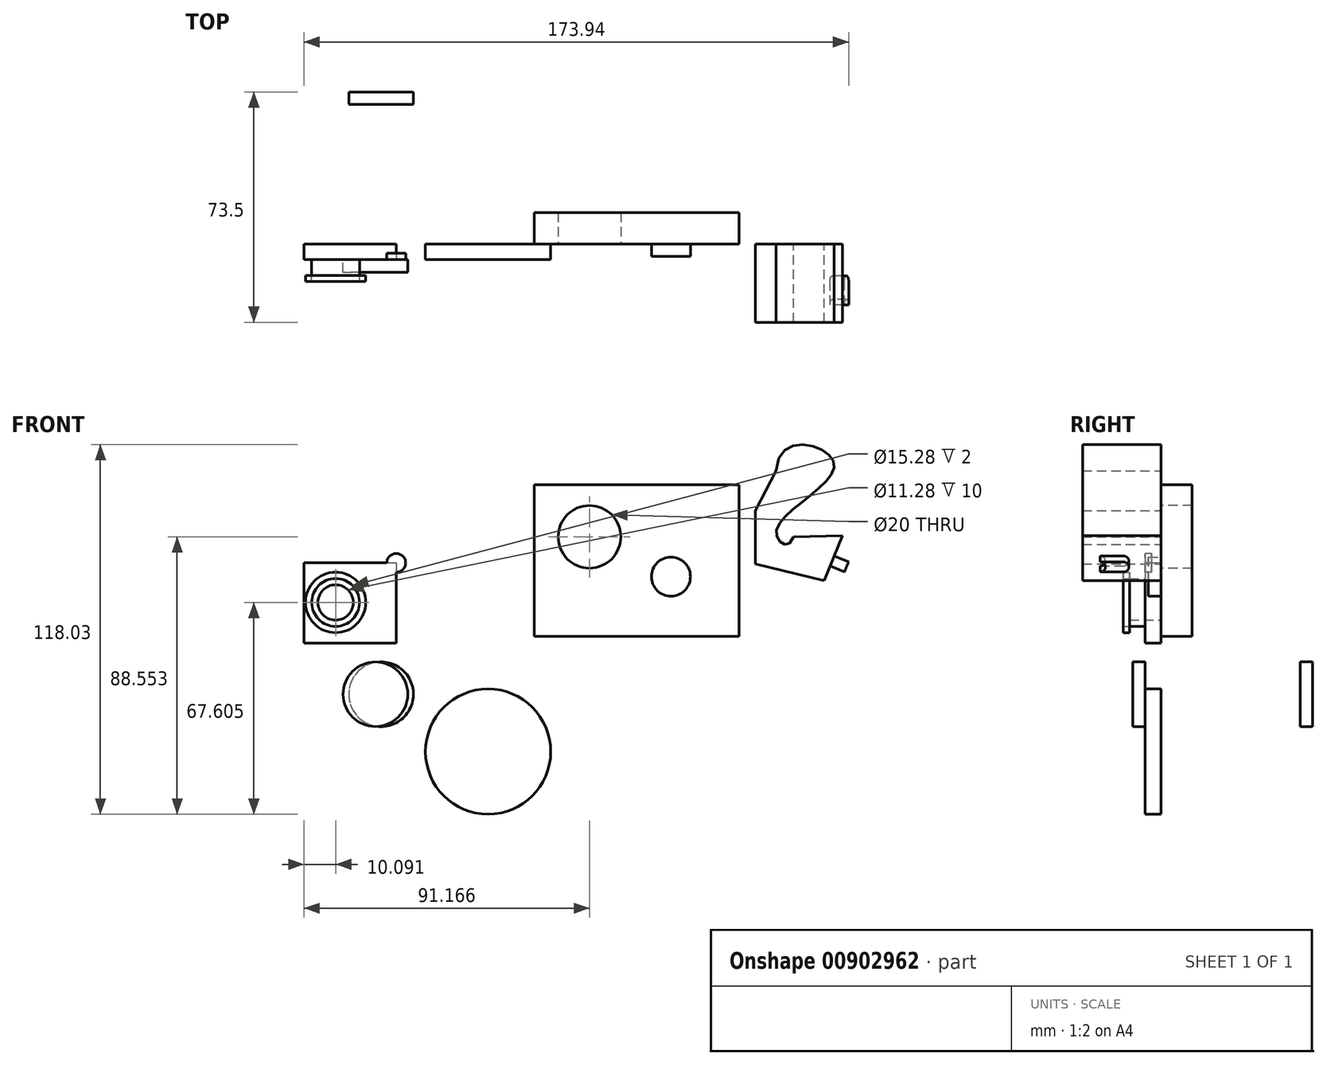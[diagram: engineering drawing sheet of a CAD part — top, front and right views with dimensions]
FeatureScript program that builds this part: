
annotation { "Feature Type Name" : "Feature", "Feature Type Description" : "" }
export const myFeature = defineFeature(function(context is Context, id is Id, definition is map)
    precondition{}
    {
        {
            var Q0;
            Q0=qCreatedBy(makeId("Front.planeOp"),FACE);
            var sketch = newSketch(context, id + "F0", { "sketchPlane" : qUnion([Q0])});
            skLineSegment(sketch, "E0.bottom", {"start": v(-53.56, 35.43) * mm, "end": v(11.78, 35.43) * mm});
            skLineSegment(sketch, "E0.top", {"start": v(-53.56, -12.9) * mm, "end": v(11.78, -12.9) * mm});
            skLineSegment(sketch, "E0.left", {"start": v(-53.56, 35.43) * mm, "end": v(-53.56, -12.9) * mm});
            skLineSegment(sketch, "E0.right", {"start": v(11.78, 35.43) * mm, "end": v(11.78, -12.9) * mm});
            skCircle(sketch, "E1", {"center": v(-35.94, 18.84) * mm, "radius": 10 * mm});
            skSolve(sketch);
        }
        {
            var Q0;
            Q0=makeQuery(id+"F0.imprint","IMPRINT",FACE,{"disambiguationData":[TD([[makeQuery(id+"F0.imprint","IMPRINT",EDGE,{"derivedFrom":sQuery(id+"F0.wireOp",EDGE,"E0.bottom")}),-1.0]])]});
            extrude(context, id + "F1", {"entities" : qUnion([Q0]), "depth" : -10 * mm, "offsetDistance" : 25 * mm});
        }
        {
            var Q0;
            Q0=qCreatedBy(makeId("Front.planeOp"),FACE);
            var sketch = newSketch(context, id + "F2", { "sketchPlane" : qUnion([Q0])});
            skCircle(sketch, "E2", {"center": v(-9.93, 6.14) * mm, "radius": 6.23 * mm});
            skSolve(sketch);
        }
        {
            var Q0;
            Q0=makeQuery(id+"F2.imprint","IMPRINT",FACE,{"disambiguationData":[TD([[makeQuery(id+"F2.imprint","IMPRINT",EDGE,{"derivedFrom":sQuery(id+"F2.wireOp",EDGE,"E2")}),1.0]])]});
            extrude(context, id + "F3", {"entities" : qUnion([Q0]), "operationType" : NewBodyOperationType.ADD, "depth" : 4 * mm, "offsetDistance" : 25 * mm});
        }
        {
            var Q0;
            Q0=qCreatedBy(makeId("Front.planeOp"),FACE);
            var sketch = newSketch(context, id + "F4", { "sketchPlane" : qUnion([Q0])});
            skFitSpline(sketch, "E3", {"points": [v(29.19, 18.84) * mm, v(23.66, 20.07) * mm, v(42.09, 42.6) * mm, v(23.66, 39.94) * mm], "startDerivative": vector(-20.54, -69.85) * mm, "endDerivative": vector(-5.4, -109.98) * mm});
            skLineSegment(sketch, "E4", {"start": v(23.66, 39.94) * mm, "end": v(17.05, 27.24) * mm});
            skLineSegment(sketch, "E5", {"start": v(17.05, 27.24) * mm, "end": v(17.05, 10.24) * mm});
            skLineSegment(sketch, "E6", {"start": v(17.05, 10.24) * mm, "end": v(38.96, 4.92) * mm});
            skLineSegment(sketch, "E7", {"start": v(38.96, 4.92) * mm, "end": v(44.9, 19.25) * mm});
            skLineSegment(sketch, "E8", {"start": v(44.9, 19.25) * mm, "end": v(29.19, 18.84) * mm});
            skSolve(sketch);
        }
        {
            var Q0;
            Q0=qCreatedBy(makeId("Front.planeOp"),FACE);
            var sketch = newSketch(context, id + "F5", { "sketchPlane" : qUnion([Q0])});
            skCircle(sketch, "E9", {"center": v(-68.32, -49.71) * mm, "radius": 20 * mm});
            skArc(sketch, "E10", {"start": v(38.29, -46.18) * mm, "mid": v(45.77, -34.95) * mm, "end": v(32.35, -33.48) * mm});
            skLineSegment(sketch, "E11", {"start": v(44.52, -43.53) * mm, "end": v(48.52, -43.53) * mm});
            skLineSegment(sketch, "E12", {"start": v(44.52, -43.53) * mm, "end": v(48.52, -40.53) * mm});
            skLineSegment(sketch, "E13", {"start": v(48.52, -40.53) * mm, "end": v(48.52, -43.53) * mm});
            skSolve(sketch);
        }
        {
            var Q0;
            Q0=makeQuery(id+"F4.imprint","IMPRINT",FACE,{"disambiguationData":[TD([[makeQuery(id+"F4.imprint","IMPRINT",EDGE,{"derivedFrom":sQuery(id+"F4.wireOp",EDGE,"E3")}),1.0]])]});
            extrude(context, id + "F6", {"entities" : qUnion([Q0]), "depth" : 5 * mm, "offsetDistance" : 25 * mm});
        }
        {
            var Q0;
            Q0=makeQuery(id+"F4.imprint","IMPRINT",FACE,{"disambiguationData":[TD([[makeQuery(id+"F4.imprint","IMPRINT",EDGE,{"derivedFrom":sQuery(id+"F4.wireOp",EDGE,"E3")}),1.0]])]});
            extrude(context, id + "F7", {"entities" : qUnion([Q0]), "operationType" : NewBodyOperationType.ADD, "depth" : 25 * mm, "offsetDistance" : 25 * mm});
        }
        {
            var Q0;
            {var subQ0=sQuery(id+"F4.wireOp",EDGE,"E7");Q0=makeQuery(id+"F7.boolean.opBoolean","MERGE",FACE,{"derivedFrom":[makeQuery(id+"F6.opExtrude","SWEPT_FACE",FACE,{"disambiguationData":[OSD([subQ0])]}),makeQuery(id+"F7.opExtrude","SWEPT_FACE",FACE,{"disambiguationData":[OSD([subQ0])]})]});}
            var sketch = newSketch(context, id + "F8", { "sketchPlane" : qUnion([Q0])});
            skLineSegment(sketch, "E14.bottom", {"start": v(-19.43, 27.93) * mm, "end": v(-11.94, 27.93) * mm});
            skLineSegment(sketch, "E14.top", {"start": v(-19.43, 24.45) * mm, "end": v(-11.94, 24.45) * mm});
            skLineSegment(sketch, "E14.right", {"start": v(-11.94, 27.93) * mm, "end": v(-11.94, 24.45) * mm});
            skArc(sketch, "E15", {"start": v(-11.94, 24.45) * mm, "mid": v(-10.2, 26.19) * mm, "end": v(-11.94, 27.93) * mm});
            skArc(sketch, "E16", {"start": v(-19.43, 24.45) * mm, "mid": v(-17.69, 26.19) * mm, "end": v(-19.43, 27.93) * mm});
            skSolve(sketch);
        }
        {
            var Q0;
            Q0=makeQuery(id+"F8.imprint","IMPRINT",FACE,{"disambiguationData":[TD([[makeQuery(id+"F8.imprint","IMPRINT",EDGE,{"derivedFrom":sQuery(id+"F8.wireOp",EDGE,"E14.right")}),1.0]])]});
            var Q1;
            Q1=makeQuery(id+"F8.imprint","IMPRINT",FACE,{"disambiguationData":[TD([[makeQuery(id+"F8.imprint","IMPRINT",EDGE,{"derivedFrom":sQuery(id+"F8.wireOp",EDGE,"E14.bottom")}),-1.0]])]});
            extrude(context, id + "F9", {"entities" : qUnion([Q0, Q1]), "operationType" : NewBodyOperationType.ADD, "depth" : 5 * mm, "offsetDistance" : 25 * mm});
        }
        {
            var Q0;
            Q0=qCreatedBy(makeId("Front.planeOp"),FACE);
            var sketch = newSketch(context, id + "F10", { "sketchPlane" : qUnion([Q0])});
            skLineSegment(sketch, "E17", {"start": v(-73.05, 50.1) * mm, "end": v(-17.22, 50.1) * mm});
            skPoint(sketch, "E18", {"position": v(-45.13, 50.1) * mm});
            skLineSegment(sketch, "E19", {"start": v(-17.22, 50.1) * mm, "end": v(-13.4, 59.93) * mm});
            skLineSegment(sketch, "E20.bottom", {"start": v(-73.05, 50.1) * mm, "end": v(-89.06, 50.1) * mm});
            skLineSegment(sketch, "E20.top", {"start": v(-73.05, 36.47) * mm, "end": v(-89.06, 36.47) * mm});
            skLineSegment(sketch, "E20.left", {"start": v(-73.05, 50.1) * mm, "end": v(-73.05, 36.47) * mm});
            skLineSegment(sketch, "E20.right", {"start": v(-89.06, 50.1) * mm, "end": v(-89.06, 36.47) * mm});
            skPoint(sketch, "E21", {"position": v(-81.05, 50.1) * mm});
            skPoint(sketch, "E22", {"position": v(-73.05, 43.29) * mm});
            skLineSegment(sketch, "E23", {"start": v(-89.06, 43.29) * mm, "end": v(-81.05, 36.47) * mm});
            skLineSegment(sketch, "E24", {"start": v(-81.05, 36.47) * mm, "end": v(-93.82, 21.48) * mm});
            skLineSegment(sketch, "E25", {"start": v(-89.06, 43.29) * mm, "end": v(-101.83, 28.3) * mm});
            skLineSegment(sketch, "E26", {"start": v(-93.82, 21.48) * mm, "end": v(-101.83, 28.3) * mm});
            skPoint(sketch, "E27", {"position": v(-101.83, 28.3) * mm});
            skLineSegment(sketch, "E28.bottom", {"start": v(-127.11, 10.53) * mm, "end": v(-97.65, 10.53) * mm});
            skLineSegment(sketch, "E28.top", {"start": v(-127.11, -15.1) * mm, "end": v(-97.65, -15.1) * mm});
            skLineSegment(sketch, "E28.left", {"start": v(-127.11, 10.53) * mm, "end": v(-127.11, -15.1) * mm});
            skLineSegment(sketch, "E28.right", {"start": v(-97.65, 10.53) * mm, "end": v(-97.65, -15.1) * mm});
            skCircle(sketch, "E29", {"center": v(-117.02, -2.1) * mm, "radius": 5.64 * mm});
            skSolve(sketch);
        }
        {
            var Q0;
            Q0=makeQuery(id+"F10.imprint","IMPRINT",FACE,{"disambiguationData":[TD([[makeQuery(id+"F10.imprint","IMPRINT",EDGE,{"derivedFrom":sQuery(id+"F10.wireOp",EDGE,"E28.bottom")}),-1.0]])]});
            extrude(context, id + "F11", {"entities" : qUnion([Q0]), "depth" : 5 * mm, "offsetDistance" : 25 * mm});
        }
        {
            var Q0;
            Q0=makeQuery(id+"F11.opExtrude","CAP_FACE",FACE,{"disambiguationData":[OSD([sQuery(id+"F10.wireOp",EDGE,"E28.bottom"),sQuery(id+"F10.wireOp",EDGE,"E28.top"),sQuery(id+"F10.wireOp",EDGE,"E28.left"),sQuery(id+"F10.wireOp",EDGE,"E28.right"),sQuery(id+"F10.wireOp",EDGE,"E29")])],"isStart":false});
            var sketch = newSketch(context, id + "F12", { "sketchPlane" : qUnion([Q0])});
            skCircle(sketch, "E30.0", {"center": v(-117.02, -2.1) * mm, "radius": 5.64 * mm});
            skCircle(sketch, "E31.0", {"center": v(-117.02, -2.1) * mm, "radius": 7.64 * mm});
            skSolve(sketch);
        }
        {
            var Q0;
            Q0=makeQuery(id+"F12.imprint","IMPRINT",FACE,{"disambiguationData":[TD([[makeQuery(id+"F12.imprint","IMPRINT",EDGE,{"derivedFrom":sQuery(id+"F12.wireOp",EDGE,"E30.0")}),-1.0]])]});
            extrude(context, id + "F13", {"entities" : qUnion([Q0]), "operationType" : NewBodyOperationType.ADD, "depth" : 5 * mm, "offsetDistance" : 25 * mm});
        }
        {
            var Q0;
            Q0=makeQuery(id+"F11.opExtrude","CAP_FACE",FACE,{"disambiguationData":[OSD([sQuery(id+"F10.wireOp",EDGE,"E28.bottom"),sQuery(id+"F10.wireOp",EDGE,"E28.top"),sQuery(id+"F10.wireOp",EDGE,"E28.left"),sQuery(id+"F10.wireOp",EDGE,"E28.right"),sQuery(id+"F10.wireOp",EDGE,"E29")])],"isStart":false});
            var sketch = newSketch(context, id + "F14", { "sketchPlane" : qUnion([Q0])});
            skLineSegment(sketch, "E32.bottom", {"start": v(-106.46, 5.96) * mm, "end": v(-102.52, 5.96) * mm});
            skLineSegment(sketch, "E32.top", {"start": v(-106.46, 0.96) * mm, "end": v(-102.52, 0.96) * mm});
            skLineSegment(sketch, "E32.left", {"start": v(-106.46, 5.96) * mm, "end": v(-106.46, 0.96) * mm});
            skLineSegment(sketch, "E32.right", {"start": v(-102.52, 5.96) * mm, "end": v(-102.52, 0.96) * mm});
            skLineSegment(sketch, "E33.0", {"start": v(-97.65, 10.53) * mm, "end": v(-97.65, -15.1) * mm});
            skCircle(sketch, "E34", {"center": v(-97.65, 10.53) * mm, "radius": 3 * mm});
            skArc(sketch, "E35", {"start": v(13.9, -4.64) * mm, "mid": v(21.38, 6.6) * mm, "end": v(7.96, 8.06) * mm});
            skLineSegment(sketch, "E36", {"start": v(20.13, -1.99) * mm, "end": v(24.13, -1.99) * mm});
            skLineSegment(sketch, "E37", {"start": v(20.13, -1.99) * mm, "end": v(24.13, 1.01) * mm});
            skLineSegment(sketch, "E38", {"start": v(24.13, 1.01) * mm, "end": v(24.13, -1.99) * mm});
            skSolve(sketch);
        }
        {
            var Q0;
            Q0=makeQuery(id+"F13.opExtrude","CAP_FACE",FACE,{"disambiguationData":[OSD([sQuery(id+"F12.wireOp",EDGE,"E30.0"),sQuery(id+"F12.wireOp",EDGE,"E31.0")])],"isStart":false});
            var sketch = newSketch(context, id + "F15", { "sketchPlane" : qUnion([Q0])});
            skCircle(sketch, "E39.0", {"center": v(-117.02, -2.1) * mm, "radius": 7.64 * mm});
            skCircle(sketch, "E40.0", {"center": v(-117.02, -2.1) * mm, "radius": 9.64 * mm});
            skSolve(sketch);
        }
        {
            var Q0;
            Q0=makeQuery(id+"F15.imprint","IMPRINT",FACE,{"disambiguationData":[TD([[makeQuery(id+"F15.imprint","IMPRINT",EDGE,{"derivedFrom":sQuery(id+"F15.wireOp",EDGE,"E39.0")}),-1.0]])]});
            extrude(context, id + "F16", {"entities" : qUnion([Q0]), "depth" : 2 * mm, "offsetDistance" : 25 * mm});
        }
        {
            var Q0;
            {var subQ0=sQuery(id+"F14.wireOp",EDGE,"E33.0");var subQ1=makeQuery(id+"F11.opExtrude","CAP_EDGE",EDGE,{"disambiguationData":[OSD([sQuery(id+"F10.wireOp",EDGE,"E28.bottom")])],"isStart":false});var subQ2=makeQuery(id+"F14.imprint","INTERSECT",VERTEX,{"derivedFrom":[subQ1,subQ0]});Q0=makeQuery(id+"F14.imprint","IMPRINT",FACE,{"disambiguationData":[TD([[makeQuery(id+"F14.imprint","IMPRINT",EDGE,{"disambiguationData":[TD([[subQ2,-1.0]])],"derivedFrom":subQ0}),1.0]])]});}
            extrude(context, id + "F17", {"entities" : qUnion([Q0]), "operationType" : NewBodyOperationType.ADD, "depth" : -2 * mm, "offsetDistance" : 25 * mm});
        }
        {
            var Q0;
            {var subQ0=sQuery(id+"F10.wireOp",EDGE,"E28.bottom");Q0=makeQuery(id+"F17.boolean.opBoolean","MERGE",FACE,{"derivedFrom":[makeQuery(id+"F11.opExtrude","CAP_FACE",FACE,{"disambiguationData":[OSD([subQ0,sQuery(id+"F10.wireOp",EDGE,"E28.top"),sQuery(id+"F10.wireOp",EDGE,"E28.left"),sQuery(id+"F10.wireOp",EDGE,"E28.right"),sQuery(id+"F10.wireOp",EDGE,"E29")])],"isStart":false}),makeQuery(id+"F17.opExtrude","CAP_FACE",FACE,{"disambiguationData":[OSD([subQ0,sQuery(id+"F14.wireOp",EDGE,"E33.0"),sQuery(id+"F14.wireOp",EDGE,"E34")])],"isStart":true})]});}
            var sketch = newSketch(context, id + "F18", { "sketchPlane" : qUnion([Q0])});
            skLineSegment(sketch, "E41.bottom", {"start": v(-122.82, -26.03) * mm, "end": v(-132.2, -26.03) * mm});
            skLineSegment(sketch, "E41.top", {"start": v(-128.88, -17.16) * mm, "end": v(-130.6, -17.16) * mm});
            skLineSegment(sketch, "E41.left", {"start": v(-122.82, -26.03) * mm, "end": v(-122.82, -23.22) * mm});
            skLineSegment(sketch, "E41.right", {"start": v(-132.6, -25.63) * mm, "end": v(-132.6, -19.16) * mm});
            skPoint(sketch, "E41.middle", {"position": v(-127.71, -21.6) * mm});
            skPoint(sketch, "E42.visualSharp", {"position": v(-132.6, -17.16) * mm});
            skArc(sketch, "E42.filletArc", {"start": v(-130.6, -17.16) * mm, "mid": v(-132.02, -17.75) * mm, "end": v(-132.6, -19.16) * mm});
            skPoint(sketch, "E43.visualSharp", {"position": v(-122.82, -17.16) * mm});
            skArc(sketch, "E43.filletArc", {"start": v(-122.82, -23.22) * mm, "mid": v(-124.6, -18.94) * mm, "end": v(-128.88, -17.16) * mm});
            skPoint(sketch, "E44.visualSharp", {"position": v(-132.6, -26.03) * mm});
            skArc(sketch, "E44.filletArc", {"start": v(-132.6, -25.63) * mm, "mid": v(-132.5, -25.92) * mm, "end": v(-132.2, -26.03) * mm});
            skLineSegment(sketch, "E45.0", {"start": v(-128.88, -16.46) * mm, "end": v(-130.6, -16.46) * mm});
            skLineSegment(sketch, "E46.0", {"start": v(-123.99, -24.86) * mm, "end": v(-123.99, -23.22) * mm});
            skLineSegment(sketch, "E46.1", {"start": v(-131.44, -24.86) * mm, "end": v(-131.44, -19.16) * mm});
            skArc(sketch, "E46.2", {"start": v(-130.6, -18.33) * mm, "mid": v(-131.2, -18.57) * mm, "end": v(-131.44, -19.16) * mm});
            skLineSegment(sketch, "E46.3", {"start": v(-123.99, -24.86) * mm, "end": v(-131.44, -24.86) * mm});
            skLineSegment(sketch, "E46.4", {"start": v(-128.88, -18.33) * mm, "end": v(-130.6, -18.33) * mm});
            skArc(sketch, "E46.5", {"start": v(-123.99, -23.22) * mm, "mid": v(-125.42, -19.76) * mm, "end": v(-128.88, -18.33) * mm});
            skCircle(sketch, "E47", {"center": v(-104.29, -31.4) * mm, "radius": 10.32 * mm});
            skSolve(sketch);
        }
        {
            var Q0;
            Q0=makeQuery(id+"F18.imprint","IMPRINT",FACE,{"disambiguationData":[TD([[makeQuery(id+"F18.imprint","IMPRINT",EDGE,{"derivedFrom":sQuery(id+"F18.wireOp",EDGE,"E47")}),1.0]])]});
            extrude(context, id + "F19", {"entities" : qUnion([Q0]), "depth" : 4 * mm, "offsetDistance" : 25 * mm});
        }
        {
            var Q0;
            Q0=makeQuery(id+"F5.imprint","IMPRINT",FACE,{"disambiguationData":[TD([[makeQuery(id+"F5.imprint","IMPRINT",EDGE,{"derivedFrom":sQuery(id+"F5.wireOp",EDGE,"E9")}),1.0]])]});
            extrude(context, id + "F20", {"entities" : qUnion([Q0]), "depth" : 5 * mm, "offsetDistance" : 25 * mm});
        }
        {
            var Q0;
            Q0=makeQuery(id+"F19.opExtrude","SWEPT_BODY",BODY,{"disambiguationData":[OSD([sQuery(id+"F18.wireOp",EDGE,"E47")])]});
            transform(context, id + "F21", {"entities" : qUnion([Q0]), "transformType" : TransformType.TRANSLATION_3D, "dx" : 1.8 * mm, "dy" : 53.5 * mm, "dz" : 0 * mm, "makeCopy" : true});
        }
    });
